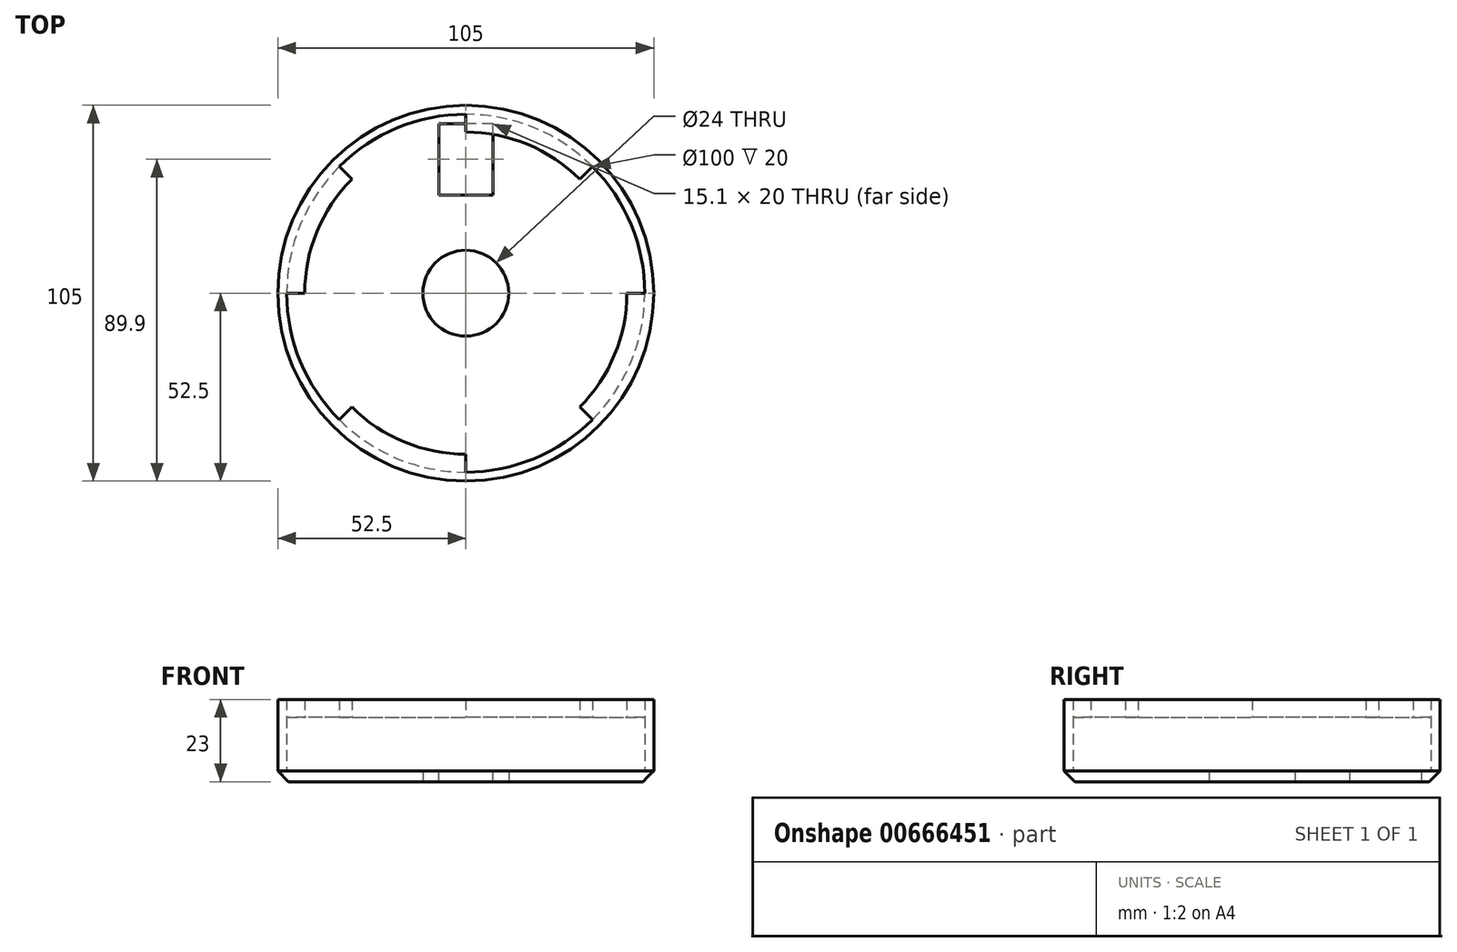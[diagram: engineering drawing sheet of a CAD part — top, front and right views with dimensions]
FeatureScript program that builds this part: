
annotation { "Feature Type Name" : "Feature", "Feature Type Description" : "" }
export const myFeature = defineFeature(function(context is Context, id is Id, definition is map)
    precondition{}
    {
        {
            var Q0;
            Q0=qCreatedBy(makeId("Top.planeOp"),FACE);
            var sketch = newSketch(context, id + "F0", { "sketchPlane" : qUnion([Q0])});
            skCircle(sketch, "E0", {"center": v(0, 0) * mm, "radius": 12 * mm});
            skCircle(sketch, "E1", {"center": v(0, 0) * mm, "radius": 50 * mm});
            skCircle(sketch, "E2", {"center": v(0, 0) * mm, "radius": 52.5 * mm});
            skLineSegment(sketch, "E3", {"start": v(0, -52.5) * mm, "end": v(0, -50) * mm});
            skSolve(sketch);
        }
        {
            var Q0;
            Q0=makeQuery(id+"F0.imprint","IMPRINT",FACE,{"disambiguationData":[TD([[makeQuery(id+"F0.imprint","IMPRINT",EDGE,{"derivedFrom":sQuery(id+"F0.wireOp",EDGE,"E0")}),-1.0]])]});
            extrude(context, id + "F1", {"entities" : qUnion([Q0]), "depth" : 3 * mm, "offsetDistance" : 25 * mm});
        }
        {
            var Q0;
            Q0=makeQuery(id+"F0.imprint","IMPRINT",FACE,{"disambiguationData":[TD([[makeQuery(id+"F0.imprint","IMPRINT",EDGE,{"derivedFrom":sQuery(id+"F0.wireOp",EDGE,"E1")}),-1.0]])]});
            extrude(context, id + "F2", {"entities" : qUnion([Q0]), "operationType" : NewBodyOperationType.ADD, "depth" : 23 * mm, "offsetDistance" : 25 * mm});
        }
        {
            var Q0;
            Q0=qCreatedBy(makeId("Top.planeOp"),FACE);
            var sketch = newSketch(context, id + "F3", { "sketchPlane" : qUnion([Q0])});
            skArc(sketch, "E4", {"start": v(35.36, -35.36) * mm, "mid": v(46.2, -19.13) * mm, "end": v(50, 0) * mm});
            skArc(sketch, "E5", {"start": v(-31.82, 31.82) * mm, "mid": v(-41.57, 17.22) * mm, "end": v(-45, 0) * mm});
            skLineSegment(sketch, "E6", {"start": v(0, 50) * mm, "end": v(0, 45) * mm});
            skLineSegment(sketch, "E7.1.0", {"start": v(-35.36, 35.36) * mm, "end": v(-31.82, 31.82) * mm});
            skLineSegment(sketch, "E7.2.0", {"start": v(-50, 0) * mm, "end": v(-45, 0) * mm});
            skLineSegment(sketch, "E7.3.0", {"start": v(-35.36, -35.36) * mm, "end": v(-31.82, -31.82) * mm});
            skLineSegment(sketch, "E7.4.0", {"start": v(0, -50) * mm, "end": v(0, -45) * mm});
            skLineSegment(sketch, "E7.5.0", {"start": v(35.36, -35.36) * mm, "end": v(31.82, -31.82) * mm});
            skLineSegment(sketch, "E7.6.0", {"start": v(50, 0) * mm, "end": v(45, 0) * mm});
            skLineSegment(sketch, "E7.7.0", {"start": v(35.36, 35.36) * mm, "end": v(31.82, 31.82) * mm});
            skArc(sketch, "E8", {"start": v(0, 50) * mm, "mid": v(19.13, 46.2) * mm, "end": v(35.36, 35.36) * mm});
            skArc(sketch, "E9", {"start": v(-35.36, 35.36) * mm, "mid": v(-46.2, 19.13) * mm, "end": v(-50, 0) * mm});
            skArc(sketch, "E10.trimOffspring", {"start": v(-31.82, -31.82) * mm, "mid": v(-17.22, -41.57) * mm, "end": v(0, -45) * mm});
            skArc(sketch, "E11.trimOffspring", {"start": v(31.82, -31.82) * mm, "mid": v(41.57, -17.22) * mm, "end": v(45, 0) * mm});
            skArc(sketch, "E12.trimOffspring", {"start": v(-35.36, -35.36) * mm, "mid": v(-19.13, -46.2) * mm, "end": v(0, -50) * mm});
            skArc(sketch, "E13.trimOffspring", {"start": v(50, 0) * mm, "mid": v(46.2, -19.13) * mm, "end": v(35.36, -35.36) * mm});
            skArc(sketch, "E14.trimOffspring", {"start": v(31.82, 31.82) * mm, "mid": v(17.22, 41.57) * mm, "end": v(0, 45) * mm});
            skArc(sketch, "E15.trimOffspring", {"start": v(35.36, 35.36) * mm, "mid": v(19.13, 46.2) * mm, "end": v(0, 50) * mm});
            skArc(sketch, "E16.trimOffspring", {"start": v(0, -50) * mm, "mid": v(-19.13, -46.2) * mm, "end": v(-35.36, -35.36) * mm});
            skSolve(sketch);
        }
        {
            var Q0;
            Q0 = qSketchRegion(id + "F3", true);
            extrude(context, id + "F4", {"entities" : qUnion([Q0]), "operationType" : NewBodyOperationType.ADD, "depth" : 23 * mm, "offsetDistance" : 25 * mm, "hasSecondDirection" : true, "secondDirectionOppositeDirection" : true, "secondDirectionDepth" : -18 * mm});
        }
        {
            var Q0;
            Q0=makeQuery(id+"F2.opExtrude","CAP_EDGE",EDGE,{"disambiguationData":[OSD([sQuery(id+"F0.wireOp",EDGE,"E2")])],"isStart":true});
            chamfer(context, id + "F5", {"entities" : qUnion([Q0]), "width" : 3 * mm, "tangentPropagation" : true});
        }
        {
            var Q0;
            Q0=makeQuery(id+"F1.opExtrude","CAP_FACE",FACE,{"disambiguationData":[OSD([sQuery(id+"F0.wireOp",EDGE,"E0"),sQuery(id+"F0.wireOp",EDGE,"E1")])],"isStart":false});
            var sketch = newSketch(context, id + "F6", { "sketchPlane" : qUnion([Q0])});
            skLineSegment(sketch, "E17.bottom", {"start": v(7.55, 27.4) * mm, "end": v(-7.55, 27.4) * mm});
            skLineSegment(sketch, "E17.top", {"start": v(7.55, 47.4) * mm, "end": v(-7.55, 47.4) * mm});
            skLineSegment(sketch, "E17.left", {"start": v(7.55, 27.4) * mm, "end": v(7.55, 47.4) * mm});
            skLineSegment(sketch, "E17.right", {"start": v(-7.55, 27.4) * mm, "end": v(-7.55, 47.4) * mm});
            skPoint(sketch, "E17.middle", {"position": v(0, 37.4) * mm});
            skSolve(sketch);
        }
        {
            var Q0;
            Q0 = qSketchRegion(id + "F6", true);
            extrude(context, id + "F7", {"entities" : qUnion([Q0]), "operationType" : NewBodyOperationType.REMOVE, "oppositeDirection" : true, "depth" : 52.8 * mm, "offsetDistance" : 25 * mm});
        }
    });
